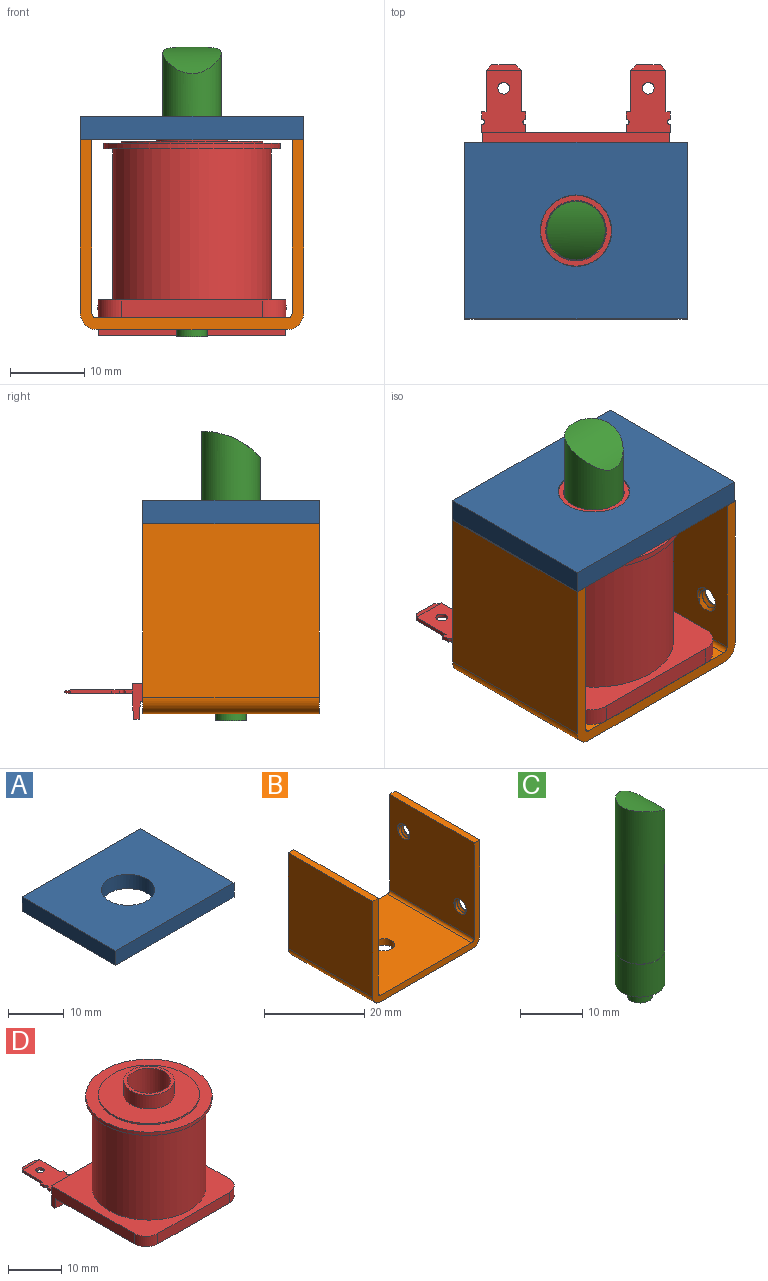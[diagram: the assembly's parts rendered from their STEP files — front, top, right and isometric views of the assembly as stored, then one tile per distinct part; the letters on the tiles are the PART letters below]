
ASSEMBLY  parts=4 mates=8
PART A: 7 faces, bbox 29.9x23.8x3.1 mm
  f0: cylinder r=4.81mm len=9.63mm, axis (0,0,1), area 95.3mm2, adj f1,f2
  f1: plane 29.95x23.77mm, normal (0,0,1), area 639.2mm2, adj f0,f3,f4,f5,f6
  f2: plane 29.95x23.77mm, normal (0,0,-1), area 639.2mm2, adj f0,f3,f4,f5,f6
  f3: plane 23.77x3.15mm, normal (-1,0,0), area 74.9mm2, adj f1,f2,f5,f6
  f4: plane 23.77x3.15mm, normal (1,0,0), area 74.9mm2, adj f1,f2,f5,f6
  f5: plane 29.95x3.15mm, normal (0,1,0), area 94.3mm2, adj f1,f2,f3,f4
  f6: plane 29.95x3.15mm, normal (0,-1,0), area 94.3mm2, adj f1,f2,f3,f4
PART B: 27 faces, bbox 30.4x23.8x25.6 mm
  f0: cone r=1.75mm half-angle=45deg, axis (1,0,0), area 3.6mm2, adj f8,f24,f25,f26
  f1: cone r=1.75mm half-angle=45deg, axis (-1,0,0), area 3.6mm2, adj f7,f24,f25,f26
  f2: cylinder r=1.75mm len=3.51mm, axis (-1,0,0), area 2.2mm2, adj f7,f8,f25,f26
  f3: cone r=1.75mm half-angle=45deg, axis (1,0,0), area 3.6mm2, adj f8,f21,f22,f23
  f4: cone r=1.75mm half-angle=45deg, axis (-1,0,0), area 3.6mm2, adj f7,f21,f22,f23
  f5: cylinder r=1.75mm len=3.51mm, axis (-1,0,0), area 2.2mm2, adj f7,f8,f22,f23
  f6: cylinder r=2.11mm len=4.22mm, axis (0,0,-1), area 20.9mm2, adj f14,f18
  f7: plane 23.77x23.37mm, normal (-1,0,0), area 536.3mm2, adj f1,f2,f4,f5,f15,f16,f19,f20
  f8: plane 23.77x23.37mm, normal (1,0,0), area 536.3mm2, adj f0,f2,f3,f5,f16,f17,f19,f20
  f9: cylinder r=2.21mm len=23.77mm, axis (0,-1,0), area 82.5mm2, adj f10,f18,f19,f20
  f10: plane 23.77x23.37mm, normal (-1,0,0), area 555.6mm2, adj f9,f11,f19,f20
  f11: plane 23.77x1.57mm, normal (0,0,1), area 37.4mm2, adj f10,f12,f19,f20
  f12: plane 23.77x23.37mm, normal (1,0,0), area 555.6mm2, adj f11,f13,f19,f20
  f13: cylinder r=0.64mm len=23.77mm, axis (0,-1,0), area 23.7mm2, adj f12,f14,f19,f20
  f14: plane 25.7x23.77mm, normal (0,0,1), area 597.2mm2, adj f6,f13,f15,f19,f20
  f15: cylinder r=0.64mm len=23.77mm, axis (0,-1,0), area 23.7mm2, adj f7,f14,f19,f20
  f16: plane 23.77x1.57mm, normal (0,0,1), area 37.4mm2, adj f7,f8,f19,f20
  f17: cylinder r=2.21mm len=23.77mm, axis (0,-1,0), area 82.5mm2, adj f8,f18,f19,f20
  f18: plane 25.7x23.77mm, normal (0,0,-1), area 597.2mm2, adj f6,f9,f17,f19,f20
  f19: plane 30.12x25.58mm, normal (0,1,0), area 121.1mm2, adj f7,f8,f9,f10,f11,f12,f13,f14
  f20: plane 30.12x25.58mm, normal (0,-1,0), area 121.1mm2, adj f7,f8,f9,f10,f11,f12,f13,f14
  f21: cylinder r=1.24mm len=2.47mm, axis (1,0,0), area 0.5mm2, adj f3,f4,f22,f23
  f22: bspline ~3.51x3.5mm, area 7.7mm2, adj f3,f4,f5,f21
  f23: bspline ~3.59x3.59mm, area 7.7mm2, adj f3,f4,f5,f21
  f24: cylinder r=1.24mm len=2.47mm, axis (1,0,0), area 0.5mm2, adj f0,f1,f25,f26
  f25: bspline ~3.51x3.5mm, area 7.7mm2, adj f0,f1,f2,f24
  f26: bspline ~3.59x3.59mm, area 7.7mm2, adj f0,f1,f2,f24
PART C: 7 faces, bbox 8x8x39 mm
  f0: cylinder r=3.98mm len=7.95mm, axis (0,0,1), area 161.1mm2, adj f4,f5
  f1: cylinder r=2.03mm len=4.06mm, axis (0,0,1), area 32.4mm2, adj f3,f4
  f2: cylinder r=3.94mm len=30.01mm, axis (0,0,1), area 711.2mm2, adj f5,f6
  f3: plane 4.06x4.06mm, normal (0,0,-1), area 13mm2, adj f1
  f4: plane 7.95x7.95mm, normal (0,0,-1), area 36.7mm2, adj f0,f1
  f5: plane 7.95x7.95mm, normal (0,0,1), area 0.9mm2, adj f0,f2
  f6: cylinder r=10.5mm len=7.88mm, axis (0,1,0), area 54.4mm2, adj f2
PART D: 59 faces, bbox 25.4x34.3x29.3 mm
  f0: cylinder r=0.79mm len=1.57mm, axis (0,0,1), area 2.5mm2, adj f53,f54
  f1: cylinder r=0.38mm len=0.76mm, axis (0,0,1), area 0.6mm2, adj f41,f42,f53,f54
  f2: cylinder r=0.79mm len=1.57mm, axis (0,0,1), area 2.5mm2, adj f38,f39
  f3: cylinder r=0.38mm len=0.76mm, axis (0,0,1), area 0.6mm2, adj f25,f26,f38,f39
  f4: cylinder r=4.77mm len=9.53mm, axis (0,0,1), area 94.3mm2, adj f23,f24
  f5: cylinder r=9.53mm len=19.05mm, axis (0,0,1), area 18.2mm2, adj f22,f23
  f6: cylinder r=11.9mm len=23.8mm, axis (0,0,1), area 57mm2, adj f21,f22
  f7: cylinder r=10.71mm len=21.41mm, axis (0,0,1), area 1368.6mm2, adj f10,f21
  f8: cylinder r=4.08mm len=26.97mm, axis (0,0,-1), area 691mm2, adj f11,f24
  f9: plane 25.27x2.41mm, normal (0,1,0), area 55mm2, adj f10,f12,f16,f20,f25,f38,f39,f52
  f10: plane 25.27x25.15mm, normal (0,0,1), area 271.1mm2, adj f7,f9,f12,f13,f14,f15,f16
  f11: plane 25.27x23.97mm, normal (0,0,-1), area 549.2mm2, adj f8,f12,f13,f14,f15,f16,f17
  f12: plane 21.97x4.78mm, normal (-1,0,0), area 55.2mm2, adj f9,f10,f11,f13,f17,f18,f19,f20
  f13: cylinder r=3.17mm len=3.18mm, axis (0,0,-1), area 12mm2, adj f10,f11,f12,f14
  f14: plane 18.92x2.41mm, normal (0,-1,0), area 45.7mm2, adj f10,f11,f13,f15
  f15: cylinder r=3.17mm len=3.18mm, axis (0,0,-1), area 12mm2, adj f10,f11,f14,f16
  f16: plane 21.97x4.78mm, normal (1,0,0), area 55.2mm2, adj f9,f10,f11,f15,f17,f18,f19,f20
  f17: cylinder r=0.15mm len=25.27mm, axis (-1,0,0), area 5.8mm2, adj f11,f12,f16,f18
  f18: plane 25.27x2.22mm, normal (0,-1,-0.05), area 56.1mm2, adj f12,f16,f17,f19
  f19: plane 25.27x0.79mm, normal (0,0,-1), area 19.9mm2, adj f12,f16,f18,f20
  f20: plane 25.27x2.36mm, normal (0,1,-0.05), area 59.8mm2, adj f9,f12,f16,f19
  f21: plane 23.8x23.8mm, normal (0,0,-1), area 84.8mm2, adj f6,f7
  f22: plane 23.8x23.8mm, normal (0,0,1), area 159.9mm2, adj f5,f6
  f23: plane 19.05x19.05mm, normal (0,0,1), area 213.7mm2, adj f4,f5
  f24: plane 9.53x9.53mm, normal (0,0,1), area 19.2mm2, adj f4,f8
  f25: plane 1.02x0.51mm, normal (-1,0,0), area 0.5mm2, adj f3,f9,f38,f39
  f26: plane 1.02x0.51mm, normal (-1,0,0), area 0.5mm2, adj f3,f27,f38,f39
  f27: plane 0.6x0.51mm, normal (0,1,0), area 0.3mm2, adj f26,f28,f38,f39
  f28: plane 5.59x0.51mm, normal (-1,0,0), area 2.8mm2, adj f27,f29,f38,f39
  f29: plane 0.76x0.76mm, normal (-0.71,0.71,0), area 0.4mm2, adj f28,f30,f56,f58
  f30: plane 3.23x0.2mm, normal (0,1,0), area 0.7mm2, adj f29,f31,f56,f58
  f31: plane 0.76x0.76mm, normal (0.71,0.71,0), area 0.4mm2, adj f30,f32,f56,f58
  f32: plane 5.59x0.51mm, normal (1,0,0), area 2.8mm2, adj f31,f33,f38,f39
  f33: plane 0.6x0.51mm, normal (0,1,0), area 0.3mm2, adj f32,f34,f38,f39
  f34: plane 1.02x0.51mm, normal (1,0,0), area 0.5mm2, adj f33,f35,f38,f39
  f35: cylinder r=0.38mm len=0.76mm, axis (0,0,1), area 0.6mm2, adj f34,f36,f38,f39
  f36: plane 1.02x0.51mm, normal (1,0,0), area 0.5mm2, adj f35,f37,f38,f39
  f37: plane 0.51x0.08mm, normal (0,-1,0), area 0mm2, adj f16,f36,f38,f39
  f38: plane 8.38x5.94mm, normal (0,0,-1), area 40.7mm2, adj f2,f3,f9,f25,f26,f27,f28,f32
  f39: plane 8.38x5.94mm, normal (0,0,1), area 40.7mm2, adj f2,f3,f9,f25,f26,f27,f28,f32
  f40: plane 0.51x0.08mm, normal (0,-1,0), area 0mm2, adj f12,f41,f53,f54
  f41: plane 1.02x0.51mm, normal (-1,0,0), area 0.5mm2, adj f1,f40,f53,f54
  f42: plane 1.02x0.51mm, normal (-1,0,0), area 0.5mm2, adj f1,f43,f53,f54
  f43: plane 0.6x0.51mm, normal (0,1,0), area 0.3mm2, adj f42,f44,f53,f54
  f44: plane 5.59x0.51mm, normal (-1,0,0), area 2.8mm2, adj f43,f45,f53,f54
  f45: plane 0.76x0.76mm, normal (-0.71,0.71,0), area 0.4mm2, adj f44,f46,f55,f57
  f46: plane 3.23x0.2mm, normal (0,1,0), area 0.7mm2, adj f45,f47,f55,f57
  f47: plane 0.76x0.76mm, normal (0.71,0.71,0), area 0.4mm2, adj f46,f48,f55,f57
  f48: plane 5.59x0.51mm, normal (1,0,0), area 2.8mm2, adj f47,f49,f53,f54
  f49: plane 0.6x0.51mm, normal (0,1,0), area 0.3mm2, adj f48,f50,f53,f54
  f50: plane 1.02x0.51mm, normal (1,0,0), area 0.5mm2, adj f49,f51,f53,f54
  f51: cylinder r=0.38mm len=0.76mm, axis (0,0,1), area 0.6mm2, adj f50,f52,f53,f54
  f52: plane 1.02x0.51mm, normal (1,0,0), area 0.5mm2, adj f9,f51,f53,f54
  f53: plane 8.38x5.94mm, normal (0,0,-1), area 40.7mm2, adj f0,f1,f9,f40,f41,f42,f43,f44
  f54: plane 8.38x5.94mm, normal (0,0,1), area 40.7mm2, adj f0,f1,f9,f40,f41,f42,f43,f44
  f55: plane 4.75x0.76mm, normal (0,0.2,0.98), area 3.1mm2, adj f45,f46,f47,f54
  f56: plane 4.75x0.76mm, normal (0,0.2,0.98), area 3.1mm2, adj f29,f30,f31,f39
  f57: plane 4.75x0.76mm, normal (0,0.2,-0.98), area 3.1mm2, adj f45,f46,f47,f53
  f58: plane 4.75x0.76mm, normal (0,0.2,-0.98), area 3.1mm2, adj f29,f30,f31,f38
PLACE A rot(axis=(0,0,1),0deg) t=(-1.55,-5.74,7.68)mm
PLACE B t=(-1.55,-5.74,7.68)mm fixed
PLACE C rot(axis=(0,0,-1),90deg) t=(-1.55,-5.74,7.68)mm
PLACE D rot(axis=(0,0,1),0deg) t=(-1.55,-5.74,7.68)mm
MATE planar B.f6 <-> C.f0  axis (0,0,1) through (-1.55,-5.74,-19.47)mm
MATE cylindrical B.f6 <-> C.f0  axis (0,0,1) through (-1.55,-5.74,-19.47)mm
MATE parallel D.f9 <-> B.f19  axis (0,1,0) through (-1.55,7.54,-17.06)mm
MATE planar A.f6 <-> B.f20  axis (0,-1,0) through (-1.55,-17.62,6.11)mm
MATE planar D.f11 <-> B.f6  axis (0,0,-1) through (-1.55,-5.53,-19.47)mm
MATE cylindrical D.f4 <-> C.f0  axis (0,0,1) through (-1.55,-5.74,-6.88)mm
MATE planar B.f11 <-> A.f0  axis (0,0,1) through (-15.82,-5.74,4.53)mm
MATE cylindrical A.f0 <-> C.f0  axis (0,0,1) through (-1.55,-5.74,6.11)mm
